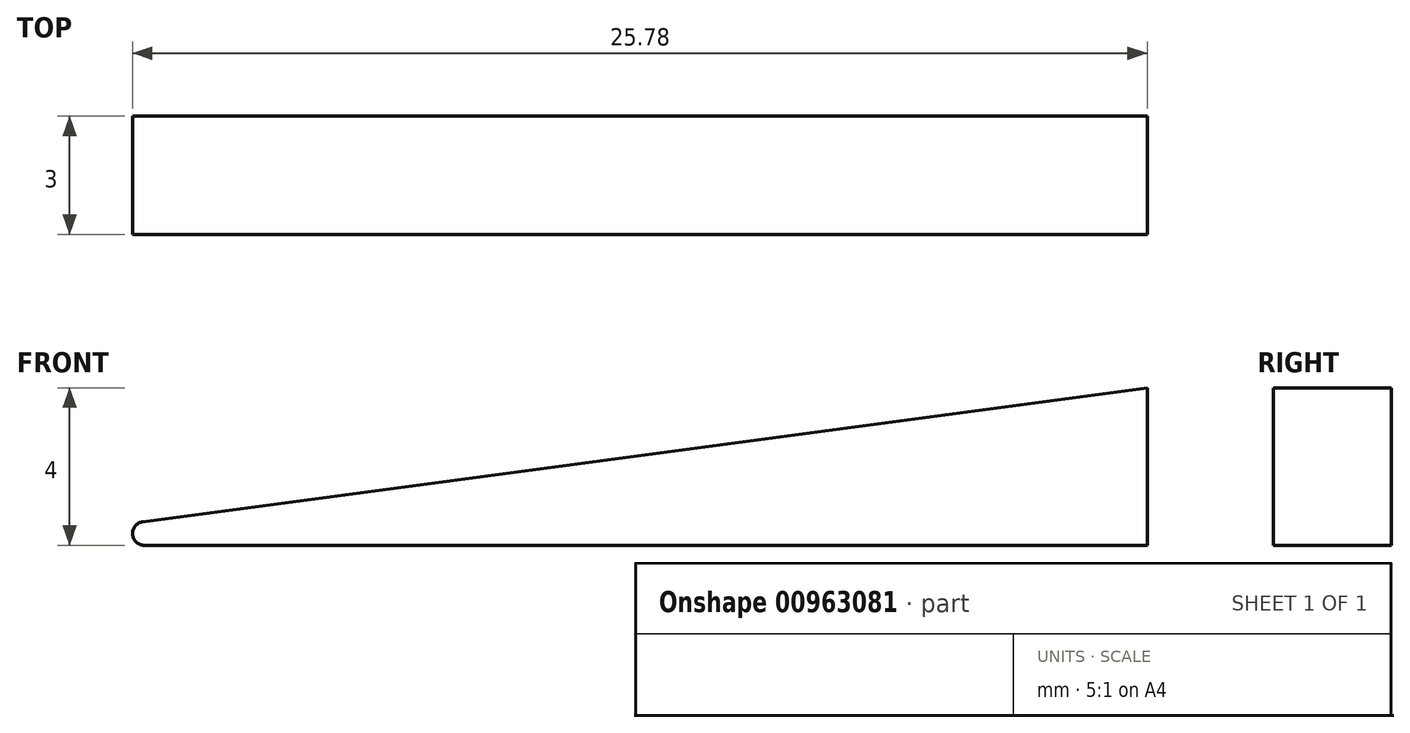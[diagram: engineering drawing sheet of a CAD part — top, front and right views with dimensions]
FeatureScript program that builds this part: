
annotation { "Feature Type Name" : "Feature", "Feature Type Description" : "" }
export const myFeature = defineFeature(function(context is Context, id is Id, definition is map)
    precondition{}
    {
        {
            var Q0;
            Q0=qCreatedBy(makeId("Top.planeOp"),FACE);
            var sketch = newSketch(context, id + "F0", { "sketchPlane" : qUnion([Q0])});
            skLineSegment(sketch, "E0.bottom", {"start": v(0, 0) * mm, "end": v(30, 0) * mm});
            skLineSegment(sketch, "E0.top", {"start": v(0, -3) * mm, "end": v(30, -3) * mm});
            skLineSegment(sketch, "E0.left", {"start": v(0, 0) * mm, "end": v(0, -3) * mm});
            skLineSegment(sketch, "E0.right", {"start": v(30, 0) * mm, "end": v(30, -3) * mm});
            skSolve(sketch);
        }
        {
            var Q0;
            Q0 = qSketchRegion(id + "F0", true);
            extrude(context, id + "F1", {"entities" : qUnion([Q0]), "depth" : 4 * mm, "offsetDistance" : 25 * mm});
        }
        {
            var Q0;
            Q0=makeQuery(id+"F1.opExtrude","SWEPT_FACE",FACE,{"disambiguationData":[OSD([sQuery(id+"F0.wireOp",EDGE,"E0.top")])]});
            var sketch = newSketch(context, id + "F2", { "sketchPlane" : qUnion([Q0])});
            skLineSegment(sketch, "E1", {"start": v(0, 0) * mm, "end": v(30, 4) * mm});
            skSolve(sketch);
        }
        {
            var Q0;
            Q0=makeQuery(id+"F2.imprint","IMPRINT",FACE,{"disambiguationData":[TD([[makeQuery(id+"F2.imprint","IMPRINT",EDGE,{"derivedFrom":sQuery(id+"F2.wireOp",EDGE,"E1")}),1.0]])]});
            extrude(context, id + "F3", {"entities" : qUnion([Q0]), "operationType" : NewBodyOperationType.REMOVE, "oppositeDirection" : true, "depth" : 25 * mm, "offsetDistance" : 25 * mm});
        }
        {
            var Q0;
            {var subQ0=sQuery(id+"F0.wireOp",EDGE,"E0.left");Q0=makeQuery(id+"F3.boolean.opBoolean","MERGE",EDGE,{"derivedFrom":[makeQuery(id+"F1.opExtrude","CAP_EDGE",EDGE,{"disambiguationData":[OSD([subQ0])],"isStart":true})],"fromTools":[makeQuery(id+"F3.opExtrude","SWEPT_EDGE",EDGE,{"disambiguationData":[OSD([sQuery(id+"F0.wireOp",EDGE,"E0.top"),subQ0,sQuery(id+"F2.wireOp",EDGE,"E1")])]})]});}
            fillet(context, id + "F4", {"entities" : qUnion([Q0]), "radius" : 0.3 * mm, "tangentPropagation" : true, "allowEdgeOverflow" : false});
        }
    });
